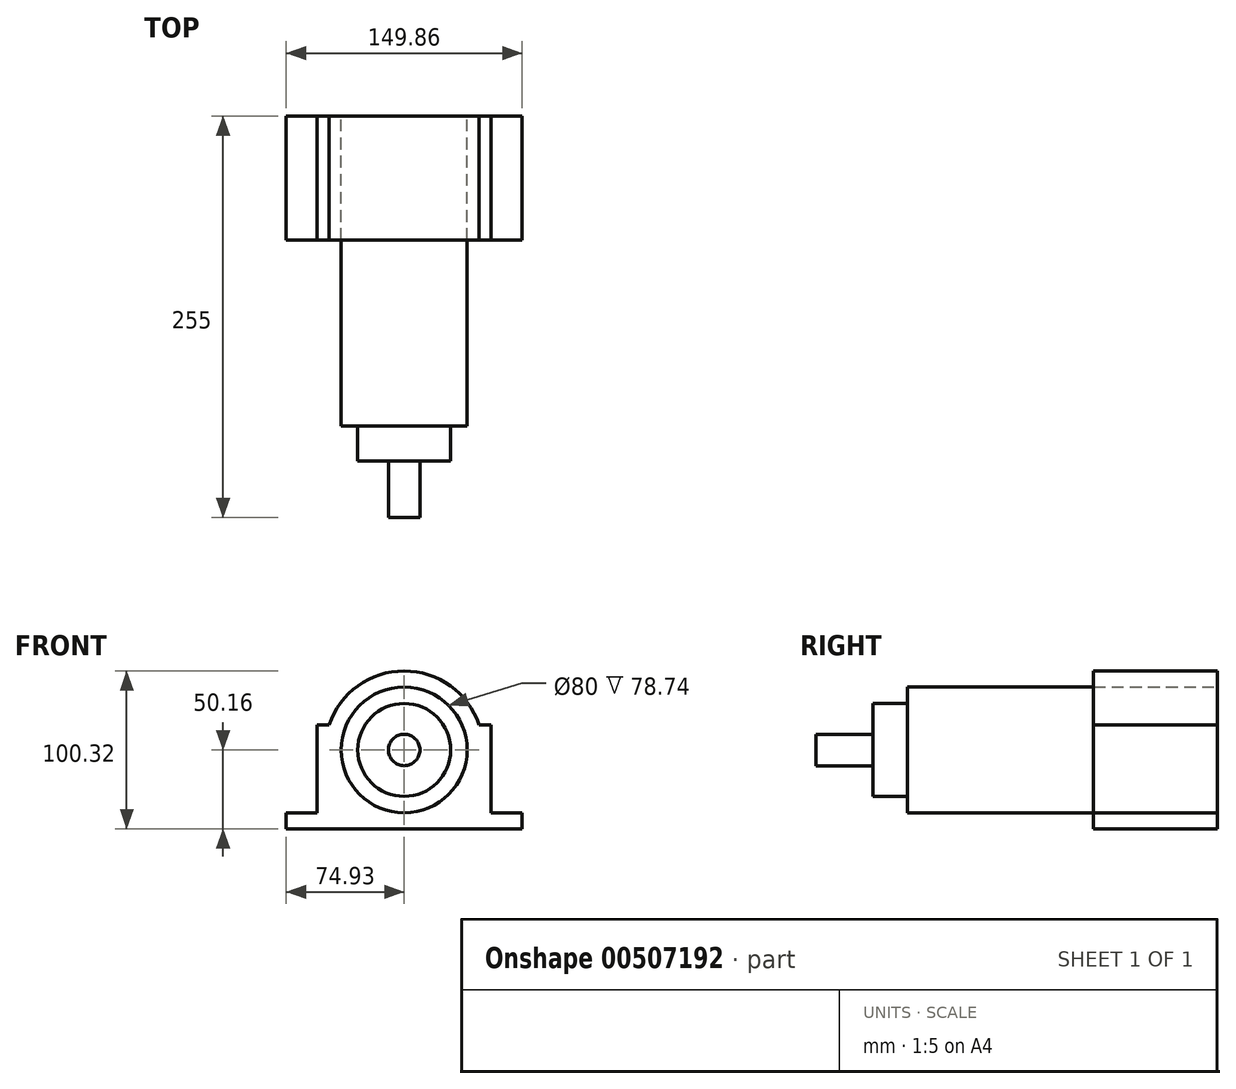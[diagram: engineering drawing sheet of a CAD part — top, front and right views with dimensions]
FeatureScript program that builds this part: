
annotation { "Feature Type Name" : "Feature", "Feature Type Description" : "" }
export const myFeature = defineFeature(function(context is Context, id is Id, definition is map)
    precondition{}
    {
        {
            var Q0;
            Q0=qCreatedBy(makeId("Front.planeOp"),FACE);
            var sketch = newSketch(context, id + "F0", { "sketchPlane" : qUnion([Q0])});
            skCircle(sketch, "E0", {"center": v(0, 0) * mm, "radius": 40 * mm});
            skSolve(sketch);
        }
        {
            var Q0;
            Q0 = qSketchRegion(id + "F0", true);
            extrude(context, id + "F1", {"entities" : qUnion([Q0]), "depth" : 197 * mm});
        }
        {
            var Q0;
            Q0=makeQuery(id+"F1.opExtrude","CAP_FACE",FACE,{"disambiguationData":[OSD([sQuery(id+"F0.wireOp",EDGE,"E0")])],"isStart":false});
            var sketch = newSketch(context, id + "F2", { "sketchPlane" : qUnion([Q0])});
            skCircle(sketch, "E1", {"center": v(0, 0) * mm, "radius": 29.5 * mm});
            skSolve(sketch);
        }
        {
            var Q0;
            Q0 = qSketchRegion(id + "F2", true);
            extrude(context, id + "F3", {"entities" : qUnion([Q0]), "operationType" : NewBodyOperationType.ADD, "depth" : 22 * mm});
        }
        {
            var Q0;
            Q0=makeQuery(id+"F3.opExtrude","CAP_FACE",FACE,{"disambiguationData":[OSD([sQuery(id+"F2.wireOp",EDGE,"E1")])],"isStart":false});
            var sketch = newSketch(context, id + "F4", { "sketchPlane" : qUnion([Q0])});
            skCircle(sketch, "E2", {"center": v(0, 0) * mm, "radius": 10 * mm});
            skSolve(sketch);
        }
        {
            var Q0;
            Q0 = qSketchRegion(id + "F4", true);
            extrude(context, id + "F5", {"entities" : qUnion([Q0]), "operationType" : NewBodyOperationType.ADD, "depth" : 36 * mm});
        }
        {
            var Q0;
            Q0=qCreatedBy(makeId("Front.planeOp"),FACE);
            var sketch = newSketch(context, id + "F6", { "sketchPlane" : qUnion([Q0])});
            skLineSegment(sketch, "E3", {"start": v(0, -50.16) * mm, "end": v(74.93, -50.16) * mm});
            skLineSegment(sketch, "E4", {"start": v(74.93, -50.16) * mm, "end": v(74.93, -40) * mm});
            skLineSegment(sketch, "E5", {"start": v(74.93, -40) * mm, "end": v(55.2, -40) * mm});
            skLineSegment(sketch, "E6", {"start": v(55.2, -40) * mm, "end": v(55.2, 15.88) * mm});
            skLineSegment(sketch, "E7", {"start": v(55.2, 15.88) * mm, "end": v(47.58, 15.88) * mm});
            skArc(sketch, "E8", {"start": v(0, 50.16) * mm, "mid": v(29.32, 40.7) * mm, "end": v(47.58, 15.88) * mm});
            skArc(sketch, "E9", {"start": v(0, 40) * mm, "mid": v(40, 0) * mm, "end": v(0, -40) * mm});
            skLineSegment(sketch, "E10.MirrorCS", {"start": v(0, -50.16) * mm, "end": v(-74.93, -50.16) * mm});
            skArc(sketch, "E11.MirrorCS", {"start": v(0, 50.16) * mm, "mid": v(-29.32, 40.7) * mm, "end": v(-47.58, 15.88) * mm});
            skLineSegment(sketch, "E12.MirrorCS", {"start": v(-74.93, -50.16) * mm, "end": v(-74.93, -40) * mm});
            skLineSegment(sketch, "E13.MirrorCS", {"start": v(-55.2, 15.88) * mm, "end": v(-47.58, 15.88) * mm});
            skArc(sketch, "E14.MirrorCS", {"start": v(0, 40) * mm, "mid": v(-40, 0) * mm, "end": v(0, -40) * mm});
            skLineSegment(sketch, "E15.MirrorCS", {"start": v(-55.2, -40) * mm, "end": v(-55.2, 15.88) * mm});
            skLineSegment(sketch, "E16.MirrorCS", {"start": v(-74.93, -40) * mm, "end": v(-55.2, -40) * mm});
            skSolve(sketch);
        }
        {
            var Q0;
            Q0 = qSketchRegion(id + "F6", true);
            extrude(context, id + "F7", {"entities" : qUnion([Q0]), "depth" : 78.74 * mm});
        }
    });
